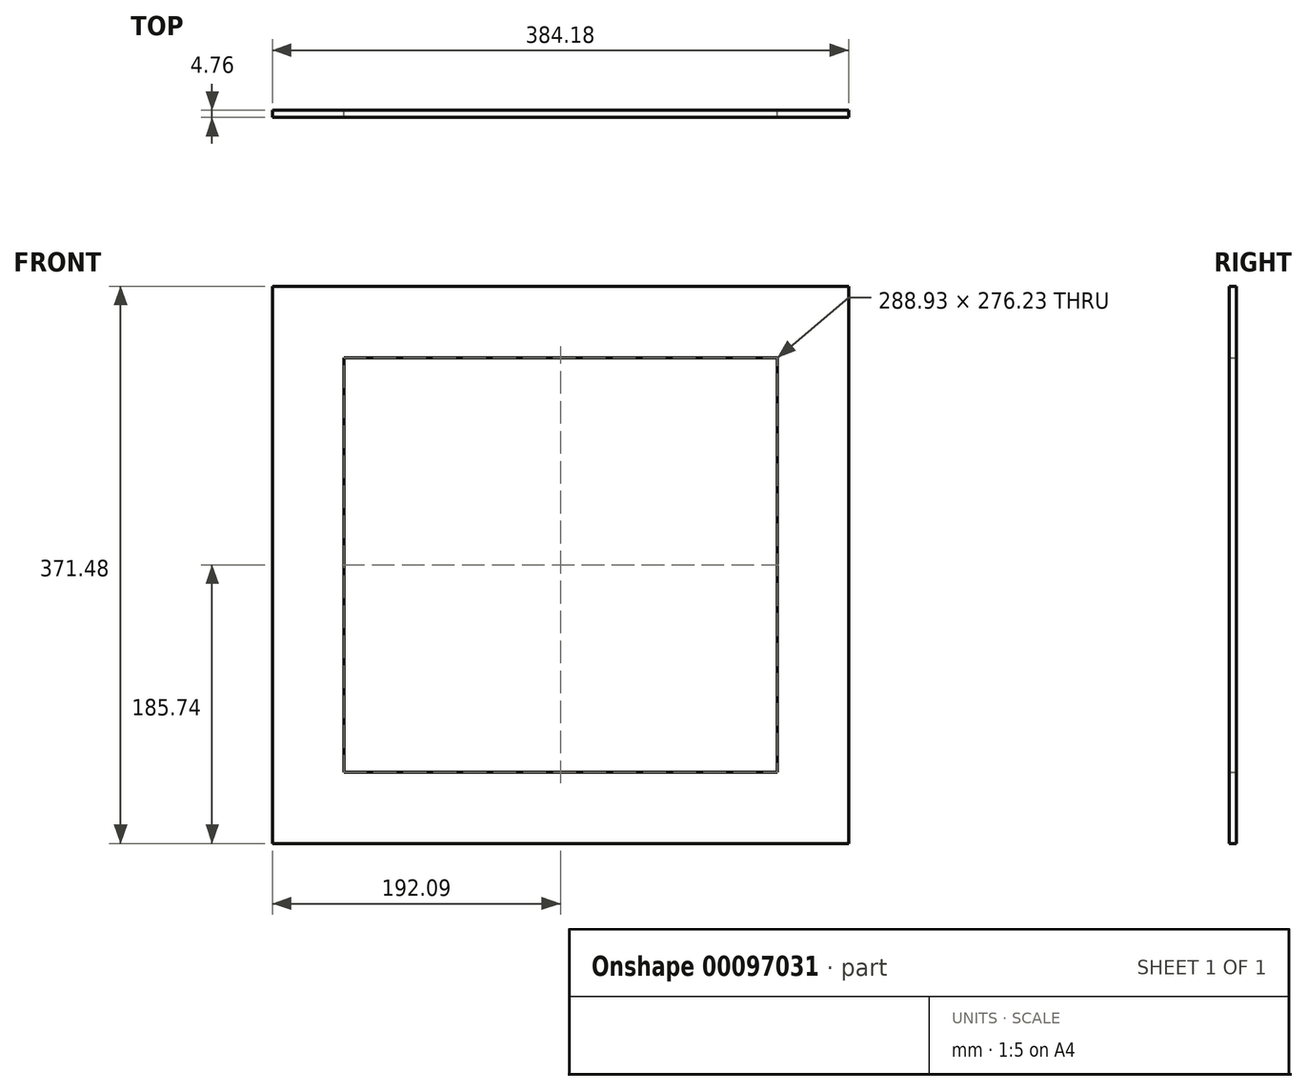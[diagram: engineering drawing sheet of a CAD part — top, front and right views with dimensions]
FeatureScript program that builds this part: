
annotation { "Feature Type Name" : "Feature", "Feature Type Description" : "" }
export const myFeature = defineFeature(function(context is Context, id is Id, definition is map)
    precondition{}
    {
        {
            var Q0;
            Q0=qCreatedBy(makeId("Front.planeOp"),FACE);
            var sketch = newSketch(context, id + "F0", { "sketchPlane" : qUnion([Q0])});
            skLineSegment(sketch, "E0.bottom", {"start": v(192.09, 185.74) * mm, "end": v(-192.09, 185.74) * mm});
            skLineSegment(sketch, "E0.top", {"start": v(192.09, -185.74) * mm, "end": v(-192.09, -185.74) * mm});
            skLineSegment(sketch, "E0.left", {"start": v(192.09, 185.74) * mm, "end": v(192.09, -185.74) * mm});
            skLineSegment(sketch, "E0.right", {"start": v(-192.09, 185.74) * mm, "end": v(-192.09, -185.74) * mm});
            skPoint(sketch, "E0.middle", {"position": v(0, 0) * mm});
            skLineSegment(sketch, "E1.0", {"start": v(144.46, 138.11) * mm, "end": v(-144.46, 138.11) * mm});
            skLineSegment(sketch, "E2.0", {"start": v(144.46, 138.11) * mm, "end": v(144.46, -138.11) * mm});
            skLineSegment(sketch, "E2.1", {"start": v(144.46, -138.11) * mm, "end": v(-144.46, -138.11) * mm});
            skLineSegment(sketch, "E2.2", {"start": v(-144.46, 138.11) * mm, "end": v(-144.46, -138.11) * mm});
            skSolve(sketch);
        }
        {
            var Q0;
            Q0=makeQuery(id+"F0.imprint","IMPRINT",FACE,{"disambiguationData":[TD([[makeQuery(id+"F0.imprint","IMPRINT",EDGE,{"derivedFrom":sQuery(id+"F0.wireOp",EDGE,"E0.bottom")}),1.0]])]});
            extrude(context, id + "F1", {"entities" : qUnion([Q0]), "endBound" : BoundingType.SYMMETRIC, "depth" : 4.76 * mm});
        }
    });
